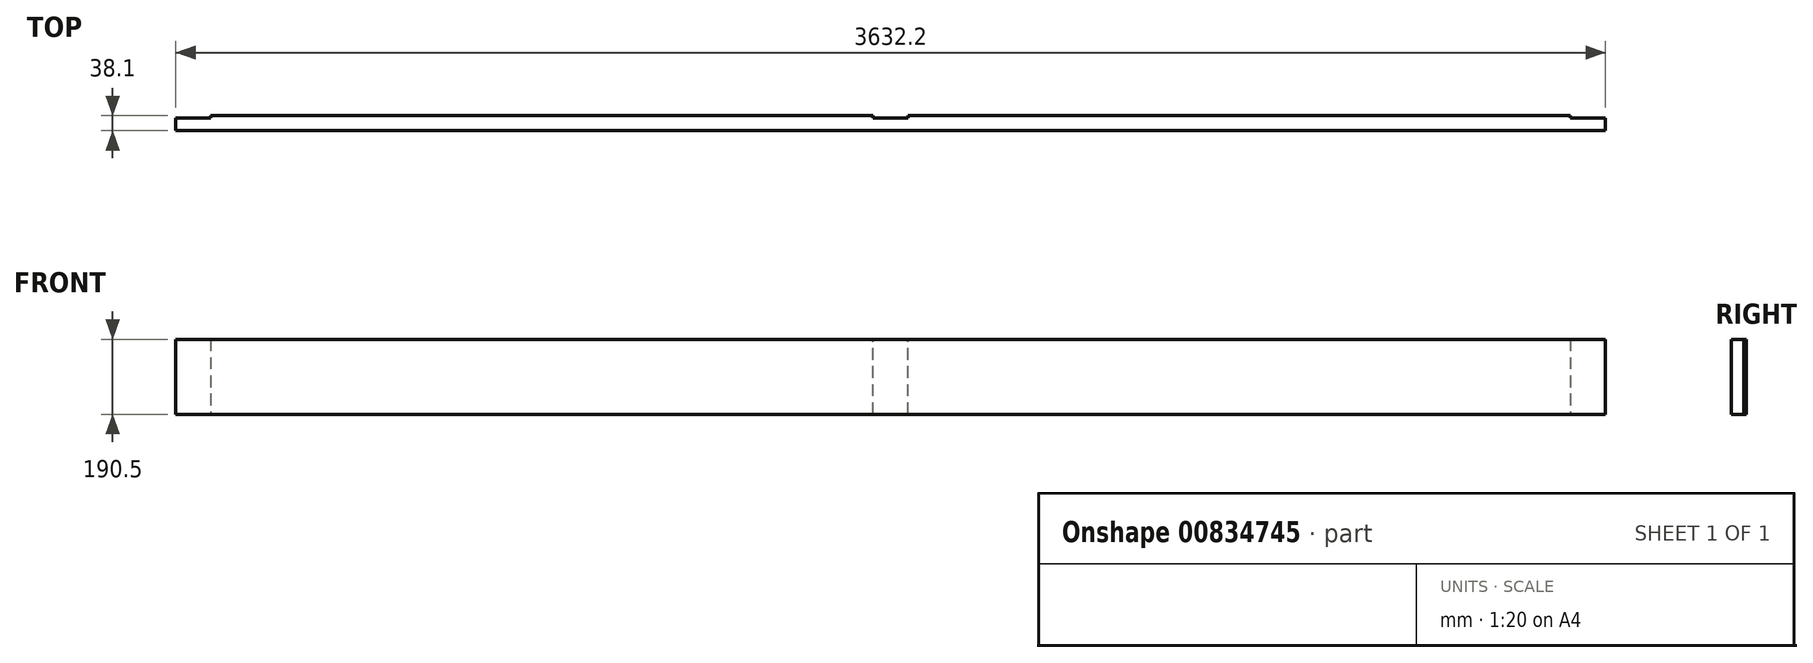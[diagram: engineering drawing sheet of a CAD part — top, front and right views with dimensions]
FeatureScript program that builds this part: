
annotation { "Feature Type Name" : "Feature", "Feature Type Description" : "" }
export const myFeature = defineFeature(function(context is Context, id is Id, definition is map)
    precondition{}
    {
        {
            var Q0;
            Q0=qCreatedBy(makeId("Front.planeOp"),FACE);
            var sketch = newSketch(context, id + "F0", { "sketchPlane" : qUnion([Q0])});
            skLineSegment(sketch, "E0.bottom", {"start": v(1816.1, -95.25) * mm, "end": v(-1816.1, -95.25) * mm});
            skLineSegment(sketch, "E0.top", {"start": v(1816.1, 95.25) * mm, "end": v(-1816.1, 95.25) * mm});
            skLineSegment(sketch, "E0.left", {"start": v(1816.1, -95.25) * mm, "end": v(1816.1, 95.25) * mm});
            skLineSegment(sketch, "E0.right", {"start": v(-1816.1, -95.25) * mm, "end": v(-1816.1, 95.25) * mm});
            skPoint(sketch, "E0.middle", {"position": v(0, 0) * mm});
            skSolve(sketch);
        }
        {
            var Q0;
            Q0 = qSketchRegion(id + "F0", true);
            extrude(context, id + "F1", {"entities" : qUnion([Q0]), "endBound" : BoundingType.SYMMETRIC, "depth" : 38.1 * mm, "offsetDistance" : 25.4 * mm});
        }
        {
            var Q0;
            Q0=makeQuery(id+"F1.opExtrude","CAP_FACE",FACE,{"disambiguationData":[OSD([sQuery(id+"F0.wireOp",EDGE,"E0.bottom"),sQuery(id+"F0.wireOp",EDGE,"E0.top"),sQuery(id+"F0.wireOp",EDGE,"E0.left"),sQuery(id+"F0.wireOp",EDGE,"E0.right")])],"isStart":true});
            var sketch = newSketch(context, id + "F2", { "sketchPlane" : qUnion([Q0])});
            skLineSegment(sketch, "E1.bottom", {"start": v(-1816.1, 95.25) * mm, "end": v(-1727.2, 95.25) * mm});
            skLineSegment(sketch, "E1.top", {"start": v(-1816.1, -95.25) * mm, "end": v(-1727.2, -95.25) * mm});
            skLineSegment(sketch, "E1.left", {"start": v(-1816.1, 95.25) * mm, "end": v(-1816.1, -95.25) * mm});
            skLineSegment(sketch, "E1.right", {"start": v(-1727.2, 95.25) * mm, "end": v(-1727.2, -95.25) * mm});
            skLineSegment(sketch, "E2.bottom", {"start": v(44.45, -95.25) * mm, "end": v(-44.45, -95.25) * mm});
            skLineSegment(sketch, "E2.top", {"start": v(44.45, 95.25) * mm, "end": v(-44.45, 95.25) * mm});
            skLineSegment(sketch, "E2.left", {"start": v(44.45, -95.25) * mm, "end": v(44.45, 95.25) * mm});
            skLineSegment(sketch, "E2.right", {"start": v(-44.45, -95.25) * mm, "end": v(-44.45, 95.25) * mm});
            skPoint(sketch, "E2.middle", {"position": v(0, 0) * mm});
            skLineSegment(sketch, "E3.MirrorCS", {"start": v(1816.1, 95.25) * mm, "end": v(1816.1, -95.25) * mm});
            skLineSegment(sketch, "E4.MirrorCS", {"start": v(1816.1, 95.25) * mm, "end": v(1727.2, 95.25) * mm});
            skLineSegment(sketch, "E5.MirrorCS", {"start": v(1816.1, -95.25) * mm, "end": v(1727.2, -95.25) * mm});
            skLineSegment(sketch, "E6.MirrorCS", {"start": v(1727.2, 95.25) * mm, "end": v(1727.2, -95.25) * mm});
            skSolve(sketch);
        }
        {
            var Q0;
            Q0 = qSketchRegion(id + "F2", true);
            extrude(context, id + "F3", {"entities" : qUnion([Q0]), "operationType" : NewBodyOperationType.REMOVE, "oppositeDirection" : true, "depth" : 6.35 * mm, "offsetDistance" : 25.4 * mm});
        }
    });
